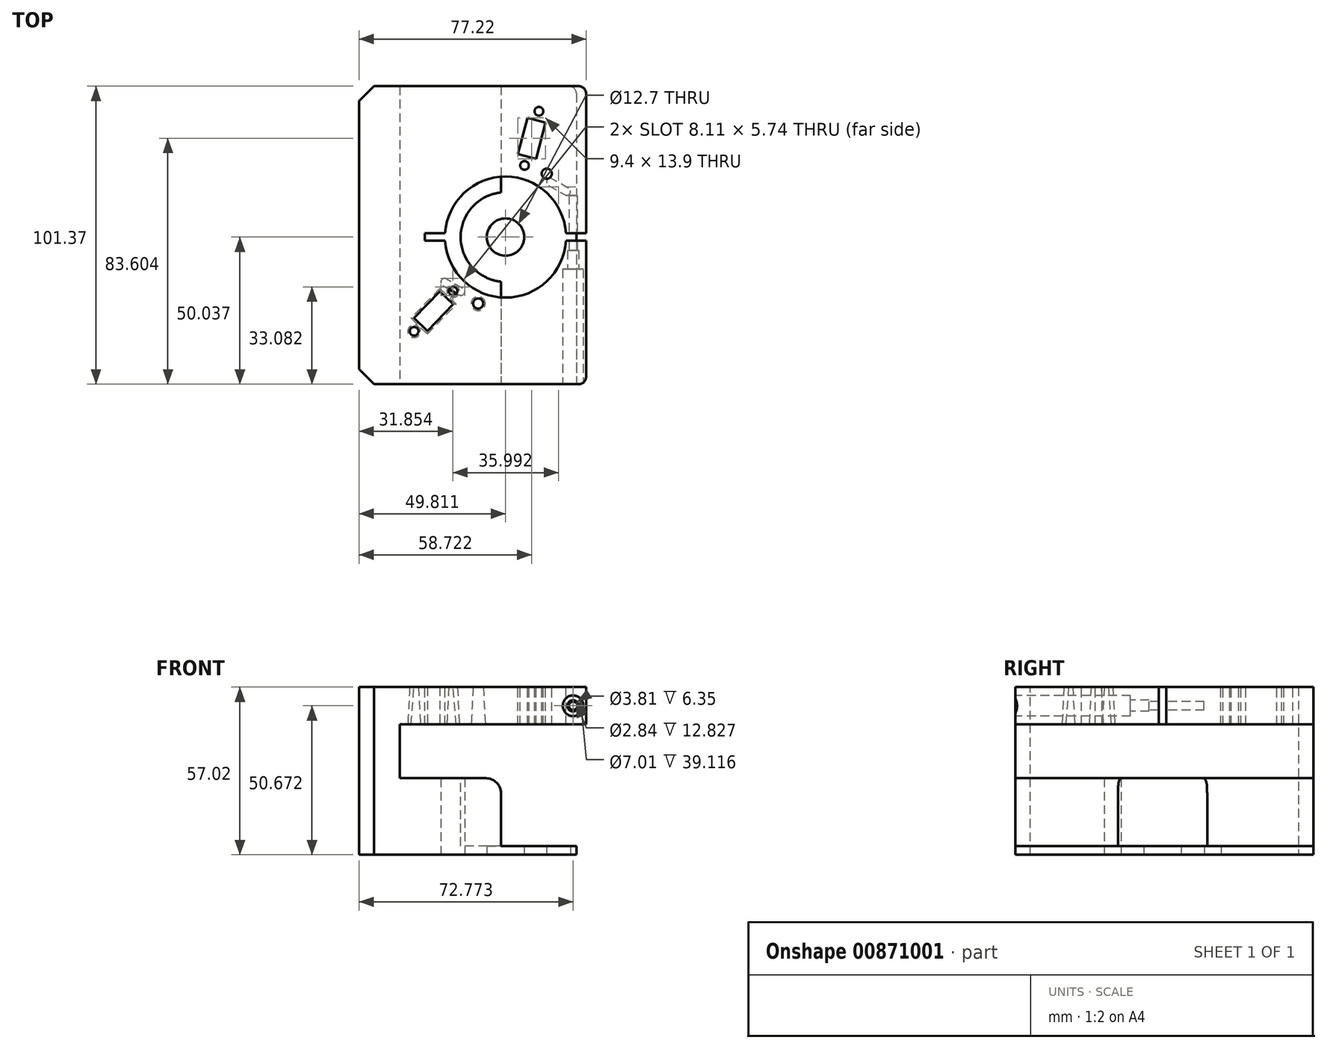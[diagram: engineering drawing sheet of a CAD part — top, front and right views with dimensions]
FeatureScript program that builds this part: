
annotation { "Feature Type Name" : "Feature", "Feature Type Description" : "" }
export const myFeature = defineFeature(function(context is Context, id is Id, definition is map)
    precondition{}
    {
        {
            var Q0;
            Q0=qCreatedBy(makeId("Front.planeOp"),FACE);
            var sketch = newSketch(context, id + "F0", { "sketchPlane" : qUnion([Q0])});
            skLineSegment(sketch, "E0.bottom", {"start": v(38.6, -28.51) * mm, "end": v(-38.6, -28.51) * mm});
            skLineSegment(sketch, "E0.top", {"start": v(38.6, 28.51) * mm, "end": v(-38.6, 28.51) * mm});
            skLineSegment(sketch, "E0.left", {"start": v(38.6, -28.51) * mm, "end": v(38.6, 28.51) * mm});
            skLineSegment(sketch, "E0.right", {"start": v(-38.6, -28.51) * mm, "end": v(-38.6, 28.51) * mm});
            skPoint(sketch, "E0.middle", {"position": v(0, 0) * mm});
            skSolve(sketch);
        }
        {
            var Q0;
            Q0=makeQuery(id+"F0.imprint","IMPRINT",FACE,{"disambiguationData":[TD([[makeQuery(id+"F0.imprint","IMPRINT",EDGE,{"derivedFrom":sQuery(id+"F0.wireOp",EDGE,"E0.bottom")}),-1.0]])]});
            extrude(context, id + "F1", {"entities" : qUnion([Q0]), "depth" : 101.37 * mm, "offsetDistance" : 25.4 * mm});
        }
        {
            var Q0;
            Q0=makeQuery(id+"F1.opExtrude","CAP_FACE",FACE,{"disambiguationData":[OSD([sQuery(id+"F0.wireOp",EDGE,"E0.bottom"),sQuery(id+"F0.wireOp",EDGE,"E0.top"),sQuery(id+"F0.wireOp",EDGE,"E0.left"),sQuery(id+"F0.wireOp",EDGE,"E0.right")])],"isStart":false});
            var sketch = newSketch(context, id + "F2", { "sketchPlane" : qUnion([Q0])});
            skSolve(sketch);
        }
        {
            var Q0;
            Q0=makeQuery(id+"F2.imprint","IMPRINT",FACE,{"disambiguationData":[TD([[makeQuery(id+"F2.imprint","IMPRINT",EDGE,{"derivedFrom":makeQuery(id+"F1.opExtrude","CAP_EDGE",EDGE,{"disambiguationData":[OSD([sQuery(id+"F0.wireOp",EDGE,"E0.bottom")])],"isStart":false})}),-1.0]])]});
            var sketch = newSketch(context, id + "F3", { "sketchPlane" : qUnion([Q0])});
            skPoint(sketch, "E1.0", {"position": v(38.6, -28.51) * mm});
            skPoint(sketch, "E2.0", {"position": v(38.6, 28.51) * mm});
            skLineSegment(sketch, "E3", {"start": v(38.6, -28.51) * mm, "end": v(35.3, -28.51) * mm});
            skLineSegment(sketch, "E4", {"start": v(35.3, -28.51) * mm, "end": v(35.3, -25.54) * mm});
            skLineSegment(sketch, "E5", {"start": v(35.3, -25.54) * mm, "end": v(9.65, -25.54) * mm});
            skLineSegment(sketch, "E6", {"start": v(9.65, -25.54) * mm, "end": v(9.65, -2.48) * mm});
            skLineSegment(sketch, "E7", {"start": v(9.65, -2.48) * mm, "end": v(-24.74, -2.48) * mm});
            skLineSegment(sketch, "E8", {"start": v(-24.74, -2.48) * mm, "end": v(-24.74, 15.81) * mm});
            skLineSegment(sketch, "E9", {"start": v(-24.74, 15.81) * mm, "end": v(38.6, 15.81) * mm});
            skLineSegment(sketch, "E10", {"start": v(38.6, 15.81) * mm, "end": v(38.6, 28.51) * mm});
            skLineSegment(sketch, "E11", {"start": v(38.6, 28.51) * mm, "end": v(57.48, 0) * mm});
            skLineSegment(sketch, "E12", {"start": v(57.48, 0) * mm, "end": v(38.6, -28.51) * mm});
            skSolve(sketch);
        }
        {
            var Q0;
            {var subQ0=sQuery(id+"F3.wireOp",EDGE,"E3");Q0=makeQuery(id+"F3.imprint","IMPRINT",FACE,{"disambiguationData":[TD([[makeQuery(id+"F3.imprint","IMPRINT",EDGE,{"derivedFrom":subQ0}),-1.0]])]});}
            extrude(context, id + "F4", {"entities" : qUnion([Q0]), "operationType" : NewBodyOperationType.REMOVE, "endBound" : BoundingType.THROUGH_ALL, "oppositeDirection" : true, "depth" : 25.4 * mm, "offsetDistance" : 25.4 * mm});
        }
        {
            var Q0;
            Q0=makeQuery(id+"F1.opExtrude","SWEPT_FACE",FACE,{"disambiguationData":[OSD([sQuery(id+"F0.wireOp",EDGE,"E0.bottom")])]});
            var sketch = newSketch(context, id + "F5", { "sketchPlane" : qUnion([Q0])});
            skSolve(sketch);
        }
        {
            var Q0;
            {var subQ0=sQuery(id+"F0.wireOp",EDGE,"E0.bottom");Q0=makeQuery(id+"F5.imprint","IMPRINT",FACE,{"disambiguationData":[TD([[makeQuery(id+"F5.imprint","IMPRINT",EDGE,{"derivedFrom":makeQuery(id+"F1.opExtrude","CAP_EDGE",EDGE,{"disambiguationData":[OSD([subQ0])],"isStart":true})}),-1.0]])]});}
            var sketch = newSketch(context, id + "F6", { "sketchPlane" : qUnion([Q0])});
            skCircle(sketch, "E13", {"center": v(11.2, 51.33) * mm, "radius": 6.35 * mm});
            skSolve(sketch);
        }
        {
            var Q0;
            Q0 = qSketchRegion(id + "F6", true);
            extrude(context, id + "F7", {"entities" : qUnion([Q0]), "operationType" : NewBodyOperationType.REMOVE, "endBound" : BoundingType.THROUGH_ALL, "oppositeDirection" : true, "depth" : 25.4 * mm, "offsetDistance" : 25.4 * mm});
        }
        {
            var Q0;
            Q0=makeQuery(id+"F4.boolean.opBoolean","COPY",FACE,{"derivedFrom":makeQuery(id+"F4.opExtrude","SWEPT_FACE",FACE,{"disambiguationData":[OSD([sQuery(id+"F3.wireOp",EDGE,"E7")])]})});
            var sketch = newSketch(context, id + "F8", { "sketchPlane" : qUnion([Q0])});
            skCircle(sketch, "E14", {"center": v(11.2, -51.33) * mm, "radius": 15.24 * mm});
            skSolve(sketch);
        }
        {
            var Q0;
            Q0 = qSketchRegion(id + "F8", true);
            var Q1;
            Q1=makeQuery(id+"F4.boolean.opBoolean","COPY",FACE,{"derivedFrom":makeQuery(id+"F4.opExtrude","SWEPT_FACE",FACE,{"disambiguationData":[OSD([sQuery(id+"F3.wireOp",EDGE,"E5")])]})});
            extrude(context, id + "F9", {"entities" : qUnion([Q0]), "operationType" : NewBodyOperationType.REMOVE, "endBound" : BoundingType.UP_TO_SURFACE, "oppositeDirection" : true, "depth" : 25.4 * mm, "endBoundEntityFace" : qUnion([Q1]), "offsetDistance" : 25.4 * mm});
        }
        {
            var Q0;
            Q0=makeQuery(id+"F1.opExtrude","SWEPT_FACE",FACE,{"disambiguationData":[OSD([sQuery(id+"F0.wireOp",EDGE,"E0.top")])]});
            var sketch = newSketch(context, id + "F10", { "sketchPlane" : qUnion([Q0])});
            skCircle(sketch, "E15", {"center": v(11.2, -51.33) * mm, "radius": 20.57 * mm});
            skSolve(sketch);
        }
        {
            var Q0;
            Q0 = qSketchRegion(id + "F10", true);
            var Q1;
            Q1=makeQuery(id+"F4.boolean.opBoolean","COPY",FACE,{"derivedFrom":makeQuery(id+"F4.opExtrude","SWEPT_FACE",FACE,{"disambiguationData":[OSD([sQuery(id+"F3.wireOp",EDGE,"E9")])]})});
            extrude(context, id + "F11", {"entities" : qUnion([Q0]), "operationType" : NewBodyOperationType.REMOVE, "endBound" : BoundingType.UP_TO_SURFACE, "oppositeDirection" : true, "depth" : 25.4 * mm, "endBoundEntityFace" : qUnion([Q1]), "offsetDistance" : 25.4 * mm});
        }
        {
            var Q0;
            Q0=makeQuery(id+"F1.opExtrude","SWEPT_FACE",FACE,{"disambiguationData":[OSD([sQuery(id+"F0.wireOp",EDGE,"E0.top")])]});
            var sketch = newSketch(context, id + "F12", { "sketchPlane" : qUnion([Q0])});
            skLineSegment(sketch, "E16.bottom", {"start": v(38.6, -52.6) * mm, "end": v(-16.2, -52.6) * mm});
            skLineSegment(sketch, "E16.top", {"start": v(38.6, -50.06) * mm, "end": v(-16.2, -50.06) * mm});
            skLineSegment(sketch, "E16.left", {"start": v(38.6, -52.6) * mm, "end": v(38.6, -50.06) * mm});
            skLineSegment(sketch, "E16.right", {"start": v(-16.2, -52.6) * mm, "end": v(-16.2, -50.06) * mm});
            skPoint(sketch, "E16.middle", {"position": v(11.2, -51.33) * mm});
            skSolve(sketch);
        }
        {
            var Q0;
            Q0 = qSketchRegion(id + "F12", true);
            var Q1;
            Q1=makeQuery(id+"F4.boolean.opBoolean","COPY",FACE,{"derivedFrom":makeQuery(id+"F4.opExtrude","SWEPT_FACE",FACE,{"disambiguationData":[OSD([sQuery(id+"F3.wireOp",EDGE,"E9")])]})});
            extrude(context, id + "F13", {"entities" : qUnion([Q0]), "operationType" : NewBodyOperationType.REMOVE, "endBound" : BoundingType.UP_TO_SURFACE, "oppositeDirection" : true, "depth" : 25.4 * mm, "endBoundEntityFace" : qUnion([Q1]), "offsetDistance" : 25.4 * mm});
        }
        {
            var Q0;
            Q0=makeQuery(id+"F1.opExtrude","CAP_EDGE",EDGE,{"disambiguationData":[OSD([sQuery(id+"F0.wireOp",EDGE,"E0.right")])],"isStart":true});
            var Q1;
            Q1=makeQuery(id+"F1.opExtrude","CAP_EDGE",EDGE,{"disambiguationData":[OSD([sQuery(id+"F0.wireOp",EDGE,"E0.right")])],"isStart":false});
            chamfer(context, id + "F14", {"entities" : qUnion([Q0, Q1]), "width" : 5.08 * mm, "tangentPropagation" : true});
        }
        {
            var Q0;
            {var subQ0=sQuery(id+"F3.wireOp",EDGE,"E6");var subQ1=sQuery(id+"F3.wireOp",EDGE,"E7");Q0=makeQuery(id+"F7.boolean.opBoolean","SPLIT",EDGE,{"disambiguationData":[TD([makeQuery(id+"F1.opExtrude","CAP_FACE",FACE,{"disambiguationData":[OSD([sQuery(id+"F0.wireOp",EDGE,"E0.bottom"),sQuery(id+"F0.wireOp",EDGE,"E0.top"),sQuery(id+"F0.wireOp",EDGE,"E0.left"),sQuery(id+"F0.wireOp",EDGE,"E0.right")])],"isStart":false})])],"derivedFrom":makeQuery(id+"F4.boolean.opBoolean","COPY",EDGE,{"derivedFrom":makeQuery(id+"F4.opExtrude","SWEPT_EDGE",EDGE,{"disambiguationData":[OSD([subQ0,subQ1])]})})});}
            var Q1;
            {var subQ0=sQuery(id+"F3.wireOp",EDGE,"E6");var subQ1=sQuery(id+"F3.wireOp",EDGE,"E7");Q1=makeQuery(id+"F7.boolean.opBoolean","SPLIT",EDGE,{"disambiguationData":[TD([makeQuery(id+"F1.opExtrude","CAP_FACE",FACE,{"disambiguationData":[OSD([sQuery(id+"F0.wireOp",EDGE,"E0.bottom"),sQuery(id+"F0.wireOp",EDGE,"E0.top"),sQuery(id+"F0.wireOp",EDGE,"E0.left"),sQuery(id+"F0.wireOp",EDGE,"E0.right")])],"isStart":true})])],"derivedFrom":makeQuery(id+"F4.boolean.opBoolean","COPY",EDGE,{"derivedFrom":makeQuery(id+"F4.opExtrude","SWEPT_EDGE",EDGE,{"disambiguationData":[OSD([subQ0,subQ1])]})})});}
            fillet(context, id + "F15", {"entities" : qUnion([Q0, Q1]), "radius" : 5.08 * mm, "tangentPropagation" : true, "allowEdgeOverflow" : false});
        }
        {
            var Q0;
            Q0=makeQuery(id+"F1.opExtrude","CAP_EDGE",EDGE,{"disambiguationData":[OSD([sQuery(id+"F0.wireOp",EDGE,"E0.left")])],"isStart":false});
            var Q1;
            Q1=makeQuery(id+"F1.opExtrude","CAP_EDGE",EDGE,{"disambiguationData":[OSD([sQuery(id+"F0.wireOp",EDGE,"E0.left")])],"isStart":true});
            var Q2;
            Q2=makeQuery(id+"F4.boolean.opBoolean","COPY",EDGE,{"derivedFrom":makeQuery(id+"F4.opExtrude","CAP_EDGE",EDGE,{"disambiguationData":[OSD([sQuery(id+"F3.wireOp",EDGE,"E4")])],"isStart":true})});
            var Q3;
            Q3=makeQuery(id+"F4.boolean.opBoolean","INTERSECT",EDGE,{"derivedFrom":[makeQuery(id+"F1.opExtrude","CAP_FACE",FACE,{"disambiguationData":[OSD([sQuery(id+"F0.wireOp",EDGE,"E0.bottom"),sQuery(id+"F0.wireOp",EDGE,"E0.top"),sQuery(id+"F0.wireOp",EDGE,"E0.left"),sQuery(id+"F0.wireOp",EDGE,"E0.right")])],"isStart":true}),makeQuery(id+"F4.opExtrude","SWEPT_FACE",FACE,{"disambiguationData":[OSD([sQuery(id+"F3.wireOp",EDGE,"E4")])]})]});
            fillet(context, id + "F16", {"entities" : qUnion([Q0, Q1, Q2, Q3]), "radius" : 2.54 * mm, "tangentPropagation" : true, "allowEdgeOverflow" : false});
        }
        {
            var Q0;
            {var subQ0=sQuery(id+"F0.wireOp",EDGE,"E0.bottom");Q0=makeQuery(id+"F5.imprint","IMPRINT",FACE,{"disambiguationData":[TD([[makeQuery(id+"F5.imprint","IMPRINT",EDGE,{"derivedFrom":makeQuery(id+"F1.opExtrude","CAP_EDGE",EDGE,{"disambiguationData":[OSD([subQ0])],"isStart":true})}),-1.0]])]});}
            var sketch = newSketch(context, id + "F17", { "sketchPlane" : qUnion([Q0])});
            skArc(sketch, "E17", {"start": v(32.66, 34.76) * mm, "mid": v(33.13, 36.5) * mm, "end": v(31.4, 36.96) * mm});
            skArc(sketch, "E18", {"start": v(25.8, 33.74) * mm, "mid": v(25.34, 32) * mm, "end": v(27.08, 31.54) * mm});
            skLineSegment(sketch, "E19", {"start": v(25.8, 33.74) * mm, "end": v(31.4, 36.96) * mm});
            skLineSegment(sketch, "E20", {"start": v(32.66, 34.76) * mm, "end": v(27.08, 31.54) * mm});
            skArc(sketch, "E21", {"start": v(-3.33, 68.8) * mm, "mid": v(-2.86, 70.54) * mm, "end": v(-4.6, 71) * mm});
            skArc(sketch, "E22", {"start": v(-10.18, 67.77) * mm, "mid": v(-10.65, 66.04) * mm, "end": v(-8.91, 65.58) * mm});
            skLineSegment(sketch, "E23", {"start": v(-10.18, 67.77) * mm, "end": v(-4.6, 71) * mm});
            skLineSegment(sketch, "E24", {"start": v(-3.33, 68.8) * mm, "end": v(-8.91, 65.58) * mm});
            skLineSegment(sketch, "E25.0.0", {"start": v(-38.6, 0) * mm, "end": v(35.3, 0) * mm});
            skLineSegment(sketch, "E25.0.2", {"start": v(35.3, 101.37) * mm, "end": v(-38.6, 101.37) * mm});
            skLineSegment(sketch, "E25.0.3", {"start": v(-38.6, 101.37) * mm, "end": v(-38.6, 0) * mm});
            skSolve(sketch);
        }
        {
            var Q0;
            Q0 = qSketchRegion(id + "F17", true);
            extrude(context, id + "F18", {"entities" : qUnion([Q0]), "operationType" : NewBodyOperationType.REMOVE, "endBound" : BoundingType.UP_TO_NEXT, "oppositeDirection" : true, "depth" : 25.4 * mm, "offsetDistance" : 25.4 * mm});
        }
        {
            var Q0;
            Q0=makeQuery(id+"F2.imprint","IMPRINT",FACE,{"disambiguationData":[TD([[makeQuery(id+"F2.imprint","IMPRINT",EDGE,{"derivedFrom":makeQuery(id+"F1.opExtrude","CAP_EDGE",EDGE,{"disambiguationData":[OSD([sQuery(id+"F0.wireOp",EDGE,"E0.bottom")])],"isStart":false})}),-1.0]])]});
            var sketch = newSketch(context, id + "F19", { "sketchPlane" : qUnion([Q0])});
            skPoint(sketch, "E26.0", {"position": v(36.07, 22.16) * mm});
            skCircle(sketch, "E27", {"center": v(34.16, 22.16) * mm, "radius": 1.42 * mm});
            skCircle(sketch, "E28", {"center": v(34.16, 22.16) * mm, "radius": 1.9 * mm});
            skCircle(sketch, "E29", {"center": v(34.16, 22.16) * mm, "radius": 3.5 * mm});
            skSolve(sketch);
        }
        {
            var Q0;
            Q0=makeQuery(id+"F19.imprint","IMPRINT",FACE,{"disambiguationData":[TD([[makeQuery(id+"F19.imprint","IMPRINT",EDGE,{"derivedFrom":sQuery(id+"F19.wireOp",EDGE,"E27")}),1.0]])]});
            extrude(context, id + "F20", {"entities" : qUnion([Q0]), "operationType" : NewBodyOperationType.REMOVE, "oppositeDirection" : true, "depth" : 64.13 * mm, "offsetDistance" : 25.4 * mm});
        }
        {
            var Q0;
            Q0=makeQuery(id+"F19.imprint","IMPRINT",FACE,{"disambiguationData":[TD([[makeQuery(id+"F19.imprint","IMPRINT",EDGE,{"derivedFrom":sQuery(id+"F19.wireOp",EDGE,"E27")}),-1.0]])]});
            extrude(context, id + "F21", {"entities" : qUnion([Q0]), "operationType" : NewBodyOperationType.REMOVE, "oppositeDirection" : true, "depth" : 45.47 * mm, "offsetDistance" : 25.4 * mm});
        }
        {
            var Q0;
            Q0=makeQuery(id+"F19.imprint","IMPRINT",FACE,{"disambiguationData":[TD([[makeQuery(id+"F19.imprint","IMPRINT",EDGE,{"derivedFrom":sQuery(id+"F19.wireOp",EDGE,"E28")}),-1.0]])]});
            extrude(context, id + "F22", {"entities" : qUnion([Q0]), "operationType" : NewBodyOperationType.REMOVE, "oppositeDirection" : true, "depth" : 39.12 * mm, "offsetDistance" : 25.4 * mm});
        }
        {
            var Q0;
            Q0=makeQuery(id+"F1.opExtrude","SWEPT_FACE",FACE,{"disambiguationData":[OSD([sQuery(id+"F0.wireOp",EDGE,"E0.top")])]});
            var sketch = newSketch(context, id + "F23", { "sketchPlane" : qUnion([Q0])});
            skCircle(sketch, "E30", {"center": v(22.56, -8.56) * mm, "radius": 1.47 * mm});
            skCircle(sketch, "E31", {"center": v(17.67, -26.97) * mm, "radius": 1.47 * mm});
            skLineSegment(sketch, "E32", {"start": v(21.74, -11.63) * mm, "end": v(24.8, -12.44) * mm});
            skLineSegment(sketch, "E33", {"start": v(24.8, -12.44) * mm, "end": v(21.55, -24.72) * mm});
            skLineSegment(sketch, "E34", {"start": v(21.55, -24.72) * mm, "end": v(18.48, -23.9) * mm});
            skLineSegment(sketch, "E35.MirrorCS", {"start": v(15.41, -23.09) * mm, "end": v(18.48, -23.9) * mm});
            skLineSegment(sketch, "E36.MirrorCS", {"start": v(18.67, -10.81) * mm, "end": v(15.41, -23.09) * mm});
            skLineSegment(sketch, "E37.MirrorCS", {"start": v(21.74, -11.63) * mm, "end": v(18.67, -10.81) * mm});
            skPoint(sketch, "E38.trimOffspring.end.orphan", {"position": v(11.2, -51.33) * mm});
            skCircle(sketch, "E39", {"center": v(25.22, -29.76) * mm, "radius": 1.73 * mm});
            skSolve(sketch);
        }
        {
            var Q0;
            Q0 = qSketchRegion(id + "F23", true);
            extrude(context, id + "F24", {"entities" : qUnion([Q0]), "operationType" : NewBodyOperationType.REMOVE, "endBound" : BoundingType.UP_TO_NEXT, "oppositeDirection" : true, "depth" : 25.4 * mm, "offsetDistance" : 25.4 * mm});
        }
        {
            var Q0;
            Q0=makeQuery(id+"F1.opExtrude","SWEPT_FACE",FACE,{"disambiguationData":[OSD([sQuery(id+"F0.wireOp",EDGE,"E0.top")])]});
            var sketch = newSketch(context, id + "F25", { "sketchPlane" : qUnion([Q0])});
            skCircle(sketch, "E40", {"center": v(-6.63, -69.7) * mm, "radius": 1.47 * mm});
            skCircle(sketch, "E41", {"center": v(-19.9, -83.37) * mm, "radius": 1.47 * mm});
            skLineSegment(sketch, "E42", {"start": v(-8.84, -71.98) * mm, "end": v(-6.56, -74.19) * mm});
            skLineSegment(sketch, "E43", {"start": v(-6.56, -74.19) * mm, "end": v(-15.41, -83.3) * mm});
            skLineSegment(sketch, "E44", {"start": v(-15.41, -83.3) * mm, "end": v(-17.69, -81.09) * mm});
            skLineSegment(sketch, "E45.MirrorCS", {"start": v(-8.84, -71.98) * mm, "end": v(-11.12, -69.76) * mm});
            skLineSegment(sketch, "E46.MirrorCS", {"start": v(-11.12, -69.76) * mm, "end": v(-19.97, -78.88) * mm});
            skLineSegment(sketch, "E47.MirrorCS", {"start": v(-19.97, -78.88) * mm, "end": v(-17.69, -81.09) * mm});
            skPoint(sketch, "E48.end.orphan", {"position": v(11.2, -51.33) * mm});
            skCircle(sketch, "E49", {"center": v(1.92, -73.92) * mm, "radius": 1.73 * mm});
            skSolve(sketch);
        }
        {
            var Q0;
            Q0 = qSketchRegion(id + "F25", true);
            extrude(context, id + "F26", {"entities" : qUnion([Q0]), "operationType" : NewBodyOperationType.REMOVE, "endBound" : BoundingType.UP_TO_NEXT, "oppositeDirection" : true, "depth" : 25.4 * mm, "offsetDistance" : 25.4 * mm, "hasDraft" : true, "draftAngle" : 3 * degree});
        }
    });
